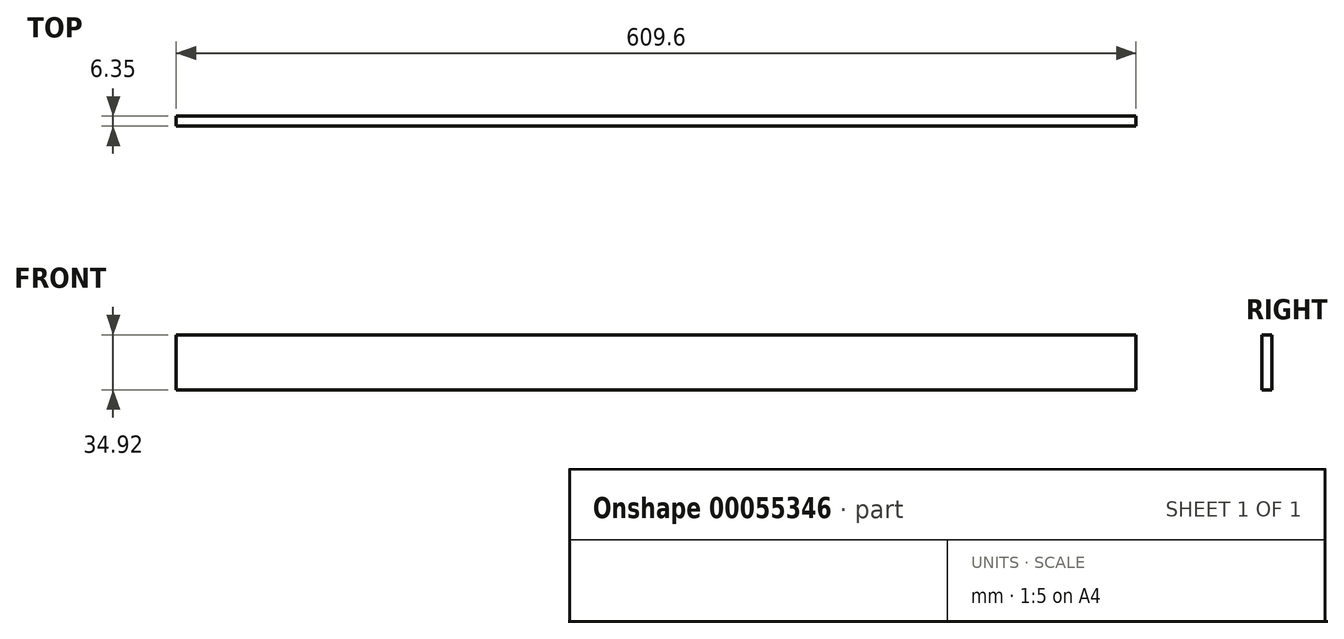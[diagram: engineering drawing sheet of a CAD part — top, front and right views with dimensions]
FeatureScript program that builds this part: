
annotation { "Feature Type Name" : "Feature", "Feature Type Description" : "" }
export const myFeature = defineFeature(function(context is Context, id is Id, definition is map)
    precondition{}
    {
        {
            var Q0;
            Q0=qCreatedBy(makeId("Front.planeOp"),FACE);
            var sketch = newSketch(context, id + "F0", { "sketchPlane" : qUnion([Q0])});
            skLineSegment(sketch, "E0.bottom", {"start": v(0, 0) * mm, "end": v(609.6, 0) * mm});
            skLineSegment(sketch, "E0.top", {"start": v(0, 34.93) * mm, "end": v(609.6, 34.93) * mm});
            skLineSegment(sketch, "E0.left", {"start": v(0, 0) * mm, "end": v(0, 34.93) * mm});
            skLineSegment(sketch, "E0.right", {"start": v(609.6, 0) * mm, "end": v(609.6, 34.93) * mm});
            skSolve(sketch);
        }
        {
            var Q0;
            Q0=qSketchRegion(id+"F0",true);
            extrude(context, id + "F1", {"entities" : qUnion([Q0]), "depth" : 6.35 * mm});
        }
    });
